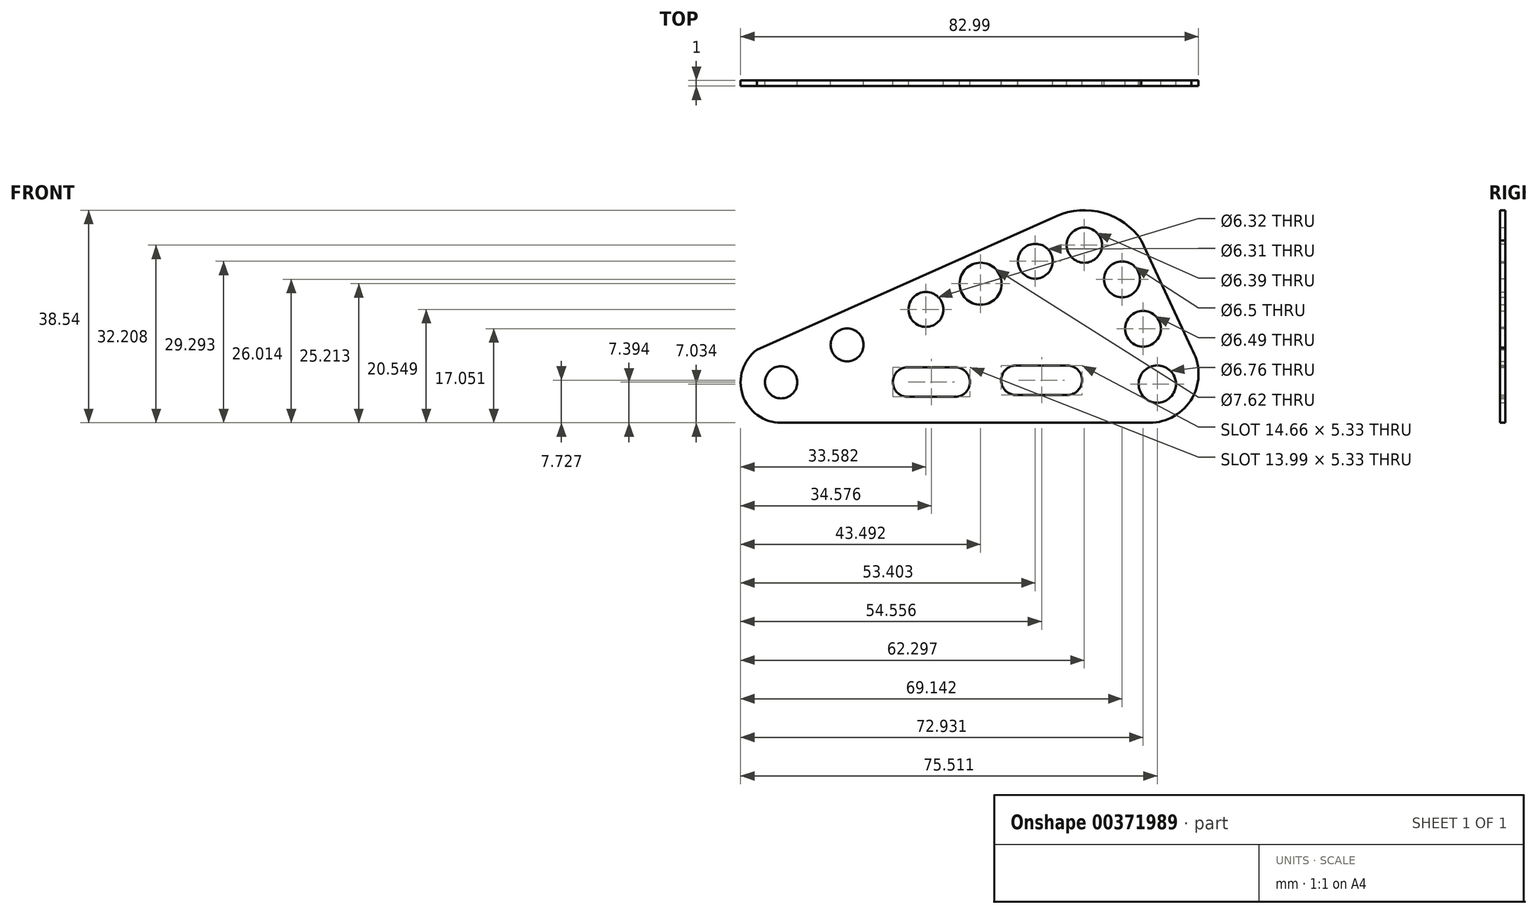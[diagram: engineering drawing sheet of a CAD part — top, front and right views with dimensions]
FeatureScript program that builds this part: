
annotation { "Feature Type Name" : "Feature", "Feature Type Description" : "" }
export const myFeature = defineFeature(function(context is Context, id is Id, definition is map)
    precondition{}
    {
        {
            var Q0;
            Q0=qCreatedBy(makeId("Front.planeOp"),FACE);
            var sketch = newSketch(context, id + "F0", { "sketchPlane" : qUnion([Q0])});
            skLineSegment(sketch, "E0", {"start": v(-11.95, 0) * mm, "end": v(54.8, 0) * mm});
            skArc(sketch, "E1", {"start": v(54.8, 0) * mm, "mid": v(62.56, 4.55) * mm, "end": v(62.38, 13.55) * mm});
            skArc(sketch, "E2", {"start": v(-11.95, 0) * mm, "mid": v(-18.93, 5.05) * mm, "end": v(-16.32, 13.26) * mm});
            skLineSegment(sketch, "E3", {"start": v(-16.32, 13.26) * mm, "end": v(37.9, 37.45) * mm});
            skArc(sketch, "E4", {"start": v(37.9, 37.45) * mm, "mid": v(46.4, 38.07) * mm, "end": v(53.34, 33.08) * mm});
            skLineSegment(sketch, "E5", {"start": v(53.34, 33.08) * mm, "end": v(62.38, 13.55) * mm});
            skCircle(sketch, "E6", {"center": v(-11.95, 7.35) * mm, "radius": 2.92 * mm});
            skCircle(sketch, "E7", {"center": v(0, 14.14) * mm, "radius": 2.98 * mm});
            skCircle(sketch, "E8", {"center": v(14.28, 20.55) * mm, "radius": 3.16 * mm});
            skCircle(sketch, "E9", {"center": v(24.2, 25.21) * mm, "radius": 3.12 * mm});
            skCircle(sketch, "E10", {"center": v(34.1, 29.3) * mm, "radius": 3.15 * mm});
            skCircle(sketch, "E11", {"center": v(43, 32.2) * mm, "radius": 3.2 * mm});
            skCircle(sketch, "E12", {"center": v(49.84, 26.01) * mm, "radius": 3.25 * mm});
            skCircle(sketch, "E13", {"center": v(53.63, 17.05) * mm, "radius": 3.25 * mm});
            skLineSegment(sketch, "E14", {"start": v(10.95, 4.73) * mm, "end": v(19.6, 4.73) * mm});
            skLineSegment(sketch, "E15", {"start": v(30.93, 5.06) * mm, "end": v(39.92, 5.06) * mm});
            skLineSegment(sketch, "E16", {"start": v(10.95, 10.06) * mm, "end": v(19.6, 10.06) * mm});
            skLineSegment(sketch, "E17", {"start": v(30.6, 10.4) * mm, "end": v(39.92, 10.4) * mm});
            skArc(sketch, "E18", {"start": v(10.95, 10.06) * mm, "mid": v(8.28, 7.4) * mm, "end": v(10.95, 4.73) * mm});
            skArc(sketch, "E19", {"start": v(19.6, 10.06) * mm, "mid": v(22.27, 7.4) * mm, "end": v(19.6, 4.73) * mm});
            skArc(sketch, "E20", {"start": v(39.92, 10.4) * mm, "mid": v(42.59, 7.73) * mm, "end": v(39.92, 5.06) * mm});
            skArc(sketch, "E21", {"start": v(30.6, 10.4) * mm, "mid": v(27.93, 7.55) * mm, "end": v(30.93, 5.06) * mm});
            skCircle(sketch, "E22", {"center": v(56.21, 7.03) * mm, "radius": 3.38 * mm});
            skSolve(sketch);
        }
        {
            var Q0;
            Q0=makeQuery(id+"F0.imprint","IMPRINT",FACE,{"disambiguationData":[TD([[makeQuery(id+"F0.imprint","IMPRINT",EDGE,{"derivedFrom":sQuery(id+"F0.wireOp",EDGE,"E0")}),1.0]])]});
            extrude(context, id + "F1", {"entities" : qUnion([Q0]), "depth" : 1 * mm});
        }
        {
            var Q0;
            Q0=sQuery(id+"F0.wireOp",VERTEX,"E9.center");
            var Q1;
            Q1=makeQuery(id+"F1.opExtrude","SWEPT_BODY",BODY,{"disambiguationData":[OSD([sQuery(id+"F0.wireOp",EDGE,"E0"),sQuery(id+"F0.wireOp",EDGE,"E1"),sQuery(id+"F0.wireOp",EDGE,"E2"),sQuery(id+"F0.wireOp",EDGE,"E3"),sQuery(id+"F0.wireOp",EDGE,"E4"),sQuery(id+"F0.wireOp",EDGE,"E5"),sQuery(id+"F0.wireOp",EDGE,"E6"),sQuery(id+"F0.wireOp",EDGE,"E7"),sQuery(id+"F0.wireOp",EDGE,"E8"),sQuery(id+"F0.wireOp",EDGE,"E9"),sQuery(id+"F0.wireOp",EDGE,"E10"),sQuery(id+"F0.wireOp",EDGE,"E11"),sQuery(id+"F0.wireOp",EDGE,"E12"),sQuery(id+"F0.wireOp",EDGE,"E13"),sQuery(id+"F0.wireOp",EDGE,"E14"),sQuery(id+"F0.wireOp",EDGE,"E15"),sQuery(id+"F0.wireOp",EDGE,"E16"),sQuery(id+"F0.wireOp",EDGE,"E17"),sQuery(id+"F0.wireOp",EDGE,"E18"),sQuery(id+"F0.wireOp",EDGE,"E19"),sQuery(id+"F0.wireOp",EDGE,"E20"),sQuery(id+"F0.wireOp",EDGE,"E21"),sQuery(id+"F0.wireOp",EDGE,"E22")])]});
            hole(context, id + "F2", {"style" : HoleStyle.SIMPLE, "endStyle" : HoleEndStyle.THROUGH, "oppositeDirection" : true, "holeDiameter" : 7.62 * mm, "isTappedThrough" : true, "tappedDepth" : 12.7 * mm, "tapClearance" : 3, "locations" : qUnion([Q0]), "scope" : qUnion([Q1])});
        }
    });
